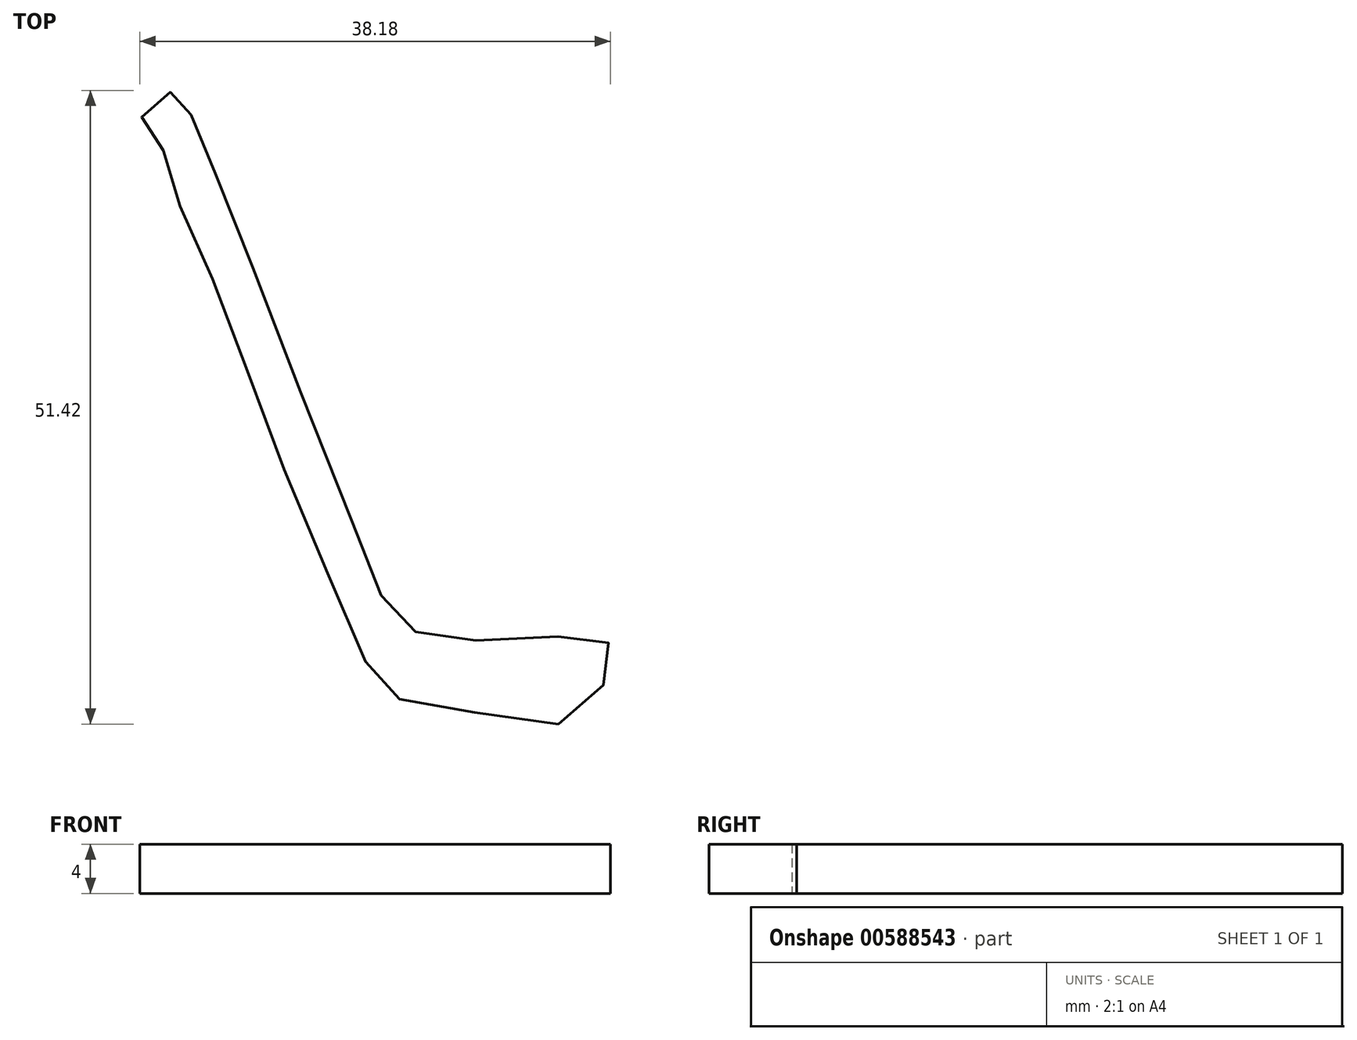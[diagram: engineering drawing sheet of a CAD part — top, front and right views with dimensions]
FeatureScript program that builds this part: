
annotation { "Feature Type Name" : "Feature", "Feature Type Description" : "" }
export const myFeature = defineFeature(function(context is Context, id is Id, definition is map)
    precondition{}
    {
        {
            var Q0;
            Q0=qCreatedBy(makeId("Top.planeOp"),FACE);
            var sketch = newSketch(context, id + "F0", { "sketchPlane" : qUnion([Q0])});
            skFitSpline(sketch, "E0", {"points": [v(-41.84, 41.58) * mm, v(-39.15, 35.57) * mm, v(-35.62, 26.03) * mm, v(-31.17, 14.84) * mm, v(-26.92, 4.9) * mm, v(-25.47, 2.3) * mm, v(-21.94, 1.06) * mm, v(-14.69, 0) * mm, v(-9.2, 0) * mm, v(-7.23, 3.54) * mm, v(-6.92, 5.4) * mm, v(-7.23, 6.34) * mm, v(-9.5, 6.65) * mm, v(-15.93, 6.45) * mm, v(-21.32, 6.45) * mm, v(-23.5, 7.59) * mm, v(-25.26, 9.55) * mm, v(-27.33, 14.53) * mm, v(-34.28, 32.15) * mm, v(-38.73, 43.65) * mm, v(-40.9, 48.62) * mm, v(-41.01, 49.45) * mm, v(-41.84, 50.9) * mm, v(-43.3, 50.6) * mm, v(-45.05, 49.87) * mm, v(-44.33, 47.7) * mm, v(-43.91, 47.48) * mm, v(-42.67, 44.48) * mm, v(-41.84, 41.58) * mm]});
            skSolve(sketch);
        }
        {
            var Q0;
            Q0=makeQuery(id+"F0.imprint","IMPRINT",FACE,{"disambiguationData":[TD([[makeQuery(id+"F0.imprint","IMPRINT",EDGE,{"derivedFrom":sQuery(id+"F0.wireOp",EDGE,"E0")}),1.0]])]});
            extrude(context, id + "F1", {"entities" : qUnion([Q0]), "depth" : 4 * mm, "offsetDistance" : 25 * mm});
        }
    });
